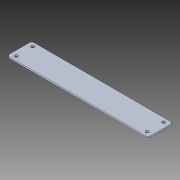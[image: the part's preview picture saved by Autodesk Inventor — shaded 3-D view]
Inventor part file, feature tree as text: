
AUTODESK INVENTOR PART (.ipt)
format: ipt  version: 2018 (Build 220112000, 112)  size: 82,432 bytes
history: native  units: in
note: dims shown in document units (in); Inventor stores cm internally (conversion verified against a paired STEP export)
features: chamfer x1
ambient origin geometry x8: Origin, YZ Plane, XZ Plane, XY Plane, X Axis, Y Axis, Z Axis, Center Point
bodies: Solid1 (feature_tree)
feature tree (1):
  chamfer  "Chamfer1"  [1 undecoded]
note: 1 required parameter value undecoded (feature->parameter linkage not recoverable at this tier; creation-order binding heuristic only, values carry confidence <= 0.55)
